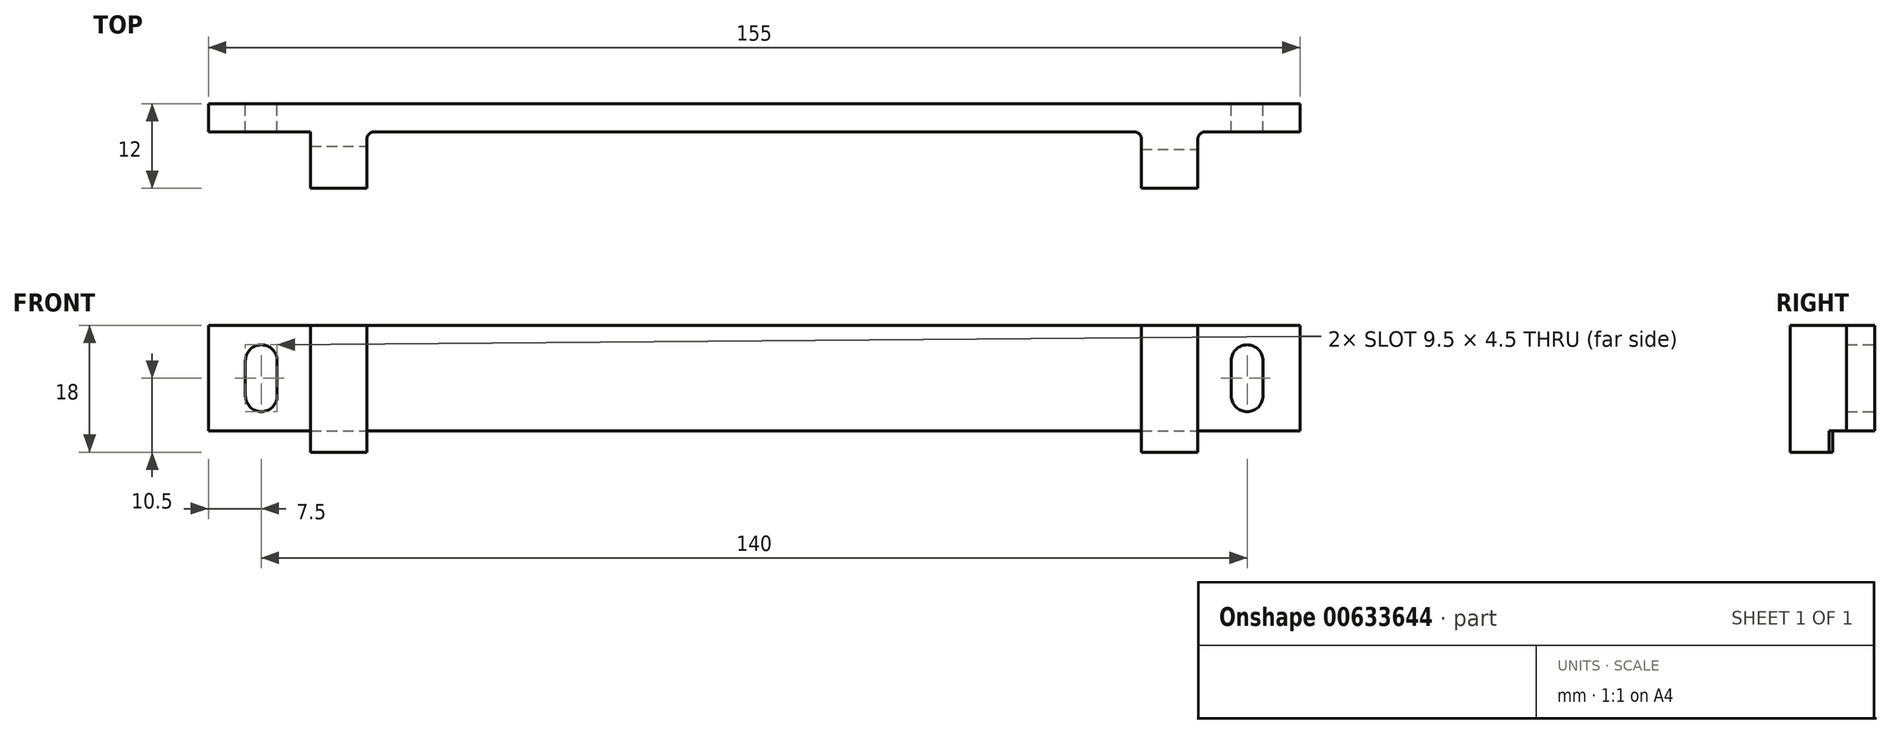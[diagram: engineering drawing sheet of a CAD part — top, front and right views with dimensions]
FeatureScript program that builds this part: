
annotation { "Feature Type Name" : "Feature", "Feature Type Description" : "" }
export const myFeature = defineFeature(function(context is Context, id is Id, definition is map)
    precondition{}
    {
        {
            var Q0;
            Q0=qCreatedBy(makeId("Front.planeOp"),FACE);
            var sketch = newSketch(context, id + "F0", { "sketchPlane" : qUnion([Q0])});
            skLineSegment(sketch, "E0.bottom", {"start": v(-77.5, 7.5) * mm, "end": v(77.5, 7.5) * mm});
            skLineSegment(sketch, "E0.top", {"start": v(-77.5, -7.5) * mm, "end": v(77.5, -7.5) * mm});
            skLineSegment(sketch, "E0.left", {"start": v(-77.5, 7.5) * mm, "end": v(-77.5, -7.5) * mm});
            skLineSegment(sketch, "E0.right", {"start": v(77.5, 7.5) * mm, "end": v(77.5, -7.5) * mm});
            skPoint(sketch, "E1.startSnap0", {"position": v(0, 7.5) * mm});
            skPoint(sketch, "E1.endSnap0", {"position": v(0, 7.5) * mm});
            skLineSegment(sketch, "E2", {"start": v(-72.25, 2.5) * mm, "end": v(-72.25, -2.5) * mm});
            skLineSegment(sketch, "E3", {"start": v(-67.75, 2.5) * mm, "end": v(-67.75, -2.5) * mm});
            skArc(sketch, "E4", {"start": v(-72.25, 2.5) * mm, "mid": v(-70, 4.75) * mm, "end": v(-67.75, 2.5) * mm});
            skArc(sketch, "E5", {"start": v(-72.25, -2.5) * mm, "mid": v(-70, -4.75) * mm, "end": v(-67.75, -2.5) * mm});
            skLineSegment(sketch, "E6.MirrorCS", {"start": v(72.25, 2.5) * mm, "end": v(72.25, -2.5) * mm});
            skArc(sketch, "E7.MirrorCS", {"start": v(72.25, 2.5) * mm, "mid": v(70, 4.75) * mm, "end": v(67.75, 2.5) * mm});
            skLineSegment(sketch, "E8.MirrorCS", {"start": v(67.75, 2.5) * mm, "end": v(67.75, -2.5) * mm});
            skArc(sketch, "E9.MirrorCS", {"start": v(72.25, -2.5) * mm, "mid": v(70, -4.75) * mm, "end": v(67.75, -2.5) * mm});
            skSolve(sketch);
        }
        {
            var Q0;
            Q0=makeQuery(id+"F0.imprint","IMPRINT",FACE,{"disambiguationData":[TD([[makeQuery(id+"F0.imprint","IMPRINT",EDGE,{"derivedFrom":sQuery(id+"F0.wireOp",EDGE,"E0.bottom")}),-1.0]])]});
            extrude(context, id + "F1", {"entities" : qUnion([Q0]), "depth" : 4 * mm, "offsetDistance" : 25 * mm});
        }
        {
            var Q0;
            Q0=makeQuery(id+"F1.opExtrude","CAP_FACE",FACE,{"disambiguationData":[OSD([sQuery(id+"F0.wireOp",EDGE,"E0.bottom"),sQuery(id+"F0.wireOp",EDGE,"E0.top"),sQuery(id+"F0.wireOp",EDGE,"E0.left"),sQuery(id+"F0.wireOp",EDGE,"E0.right"),sQuery(id+"F0.wireOp",EDGE,"ea225624-6685-4acc-8dc6-de662683e1a85.MirrorCS"),sQuery(id+"F0.wireOp",EDGE,"ea225624-6685-4acc-8dc6-de662683e1a88.MirrorCS"),sQuery(id+"F0.wireOp",EDGE,"ea225624-6685-4acc-8dc6-de662683e1a810.MirrorCS"),sQuery(id+"F0.wireOp",EDGE,"ea225624-6685-4acc-8dc6-de662683e1a813.MirrorCS"),sQuery(id+"F0.wireOp",EDGE,"ea225624-6685-4acc-8dc6-de662683e1a814.MirrorCS"),sQuery(id+"F0.wireOp",EDGE,"80049206-fc12-4322-b61f-103c15692f4b2.MirrorCS"),sQuery(id+"F0.wireOp",EDGE,"80049206-fc12-4322-b61f-103c15692f4b6.MirrorCS"),sQuery(id+"F0.wireOp",EDGE,"80049206-fc12-4322-b61f-103c15692f4b9.MirrorCS"),sQuery(id+"F0.wireOp",EDGE,"80049206-fc12-4322-b61f-103c15692f4b13.MirrorCS"),sQuery(id+"F0.wireOp",EDGE,"80049206-fc12-4322-b61f-103c15692f4b15.MirrorCS"),sQuery(id+"F0.wireOp",EDGE,"80049206-fc12-4322-b61f-103c15692f4b16.MirrorCS")])],"isStart":false});
            var sketch = newSketch(context, id + "F2", { "sketchPlane" : qUnion([Q0])});
            skLineSegment(sketch, "E10.bottom", {"start": v(-63, 7.5) * mm, "end": v(-55, 7.5) * mm});
            skLineSegment(sketch, "E10.top", {"start": v(-63, -7.5) * mm, "end": v(-55, -7.5) * mm});
            skLineSegment(sketch, "E10.left", {"start": v(-63, 7.5) * mm, "end": v(-63, -7.5) * mm});
            skLineSegment(sketch, "E10.right", {"start": v(-55, 7.5) * mm, "end": v(-55, -7.5) * mm});
            skLineSegment(sketch, "E11.MirrorCS", {"start": v(55, 7.5) * mm, "end": v(55, -7.5) * mm});
            skLineSegment(sketch, "E12.MirrorCS", {"start": v(63, -7.5) * mm, "end": v(55, -7.5) * mm});
            skLineSegment(sketch, "E13.MirrorCS", {"start": v(63, 7.5) * mm, "end": v(63, -7.5) * mm});
            skLineSegment(sketch, "E14.MirrorCS", {"start": v(63, 7.5) * mm, "end": v(55, 7.5) * mm});
            skSolve(sketch);
        }
        {
            var Q0;
            Q0=makeQuery(id+"F2.imprint","IMPRINT",FACE,{"disambiguationData":[TD([[makeQuery(id+"F2.imprint","IMPRINT",EDGE,{"derivedFrom":sQuery(id+"F2.wireOp",EDGE,"rgTuAd72-mPfx-BfAA-Xkon-aN4BqDl6kUy1.bottom")}),-1.0]])]});
            var Q1;
            Q1=makeQuery(id+"F2.imprint","IMPRINT",FACE,{"disambiguationData":[TD([[makeQuery(id+"F2.imprint","IMPRINT",EDGE,{"derivedFrom":sQuery(id+"F2.wireOp",EDGE,"rgTuAd72-mPfx-BfAA-Xkon-aN4BqDl6kUy1.top")}),1.0]])]});
            var Q2;
            Q2=makeQuery(id+"F2.imprint","IMPRINT",FACE,{"disambiguationData":[TD([[makeQuery(id+"F2.imprint","IMPRINT",EDGE,{"derivedFrom":sQuery(id+"F2.wireOp",EDGE,"E10.bottom")}),-1.0]])]});
            var Q3;
            Q3=makeQuery(id+"F2.imprint","IMPRINT",FACE,{"disambiguationData":[TD([[makeQuery(id+"F2.imprint","IMPRINT",EDGE,{"derivedFrom":sQuery(id+"F2.wireOp",EDGE,"E11.MirrorCS")}),1.0]])]});
            extrude(context, id + "F3", {"entities" : qUnion([Q0, Q1, Q2, Q3]), "operationType" : NewBodyOperationType.ADD, "depth" : 8 * mm, "offsetDistance" : 25 * mm});
        }
        {
            var Q0;
            Q0=makeQuery(id+"F3.boolean.opBoolean","MERGE",FACE,{"derivedFrom":[makeQuery(id+"F1.opExtrude","SWEPT_FACE",FACE,{"disambiguationData":[OSD([sQuery(id+"F0.wireOp",EDGE,"E0.top")])]}),makeQuery(id+"F3.opExtrude","SWEPT_FACE",FACE,{"disambiguationData":[OSD([sQuery(id+"F2.wireOp",EDGE,"rgTuAd72-mPfx-BfAA-Xkon-aN4BqDl6kUy1.top")])]})]});
            var sketch = newSketch(context, id + "F4", { "sketchPlane" : qUnion([Q0])});
            skLineSegment(sketch, "E15", {"start": v(-63, 6) * mm, "end": v(-55, 6) * mm});
            skLineSegment(sketch, "E16", {"start": v(55, 6.5) * mm, "end": v(63, 6.5) * mm});
            skSolve(sketch);
        }
        {
            var Q0;
            {var subQ0=sQuery(id+"F4.wireOp",EDGE,"E15");Q0=makeQuery(id+"F4.imprint","IMPRINT",FACE,{"disambiguationData":[TD([[makeQuery(id+"F4.imprint","IMPRINT",EDGE,{"derivedFrom":subQ0}),1.0]])]});}
            var Q1;
            {var subQ0=sQuery(id+"F4.wireOp",EDGE,"E16");Q1=makeQuery(id+"F4.imprint","IMPRINT",FACE,{"disambiguationData":[TD([[makeQuery(id+"F4.imprint","IMPRINT",EDGE,{"derivedFrom":subQ0}),1.0]])]});}
            extrude(context, id + "F5", {"entities" : qUnion([Q0, Q1]), "operationType" : NewBodyOperationType.ADD, "depth" : 3 * mm, "offsetDistance" : 25 * mm});
        }
        {
            var Q0;
            Q0=makeQuery(id+"F3.opExtrude","CAP_EDGE",EDGE,{"disambiguationData":[OSD([sQuery(id+"F2.wireOp",EDGE,"E11.MirrorCS")])],"isStart":true});
            var Q1;
            Q1=makeQuery(id+"F3.opExtrude","CAP_EDGE",EDGE,{"disambiguationData":[OSD([sQuery(id+"F2.wireOp",EDGE,"E10.right")])],"isStart":true});
            var Q2;
            Q2=makeQuery(id+"F3.opExtrude","CAP_EDGE",EDGE,{"disambiguationData":[OSD([sQuery(id+"F2.wireOp",EDGE,"E13.MirrorCS")])],"isStart":true});
            var Q3;
            Q3=makeQuery(id+"F3.opExtrude","CAP_EDGE",EDGE,{"disambiguationData":[OSD([sQuery(id+"F2.wireOp",EDGE,"E10.left")])],"isStart":true});
            fillet(context, id + "F6", {"entities" : qUnion([Q0, Q1, Q2, Q3]), "radius" : 1 * mm, "tangentPropagation" : true, "allowEdgeOverflow" : false});
        }
    });
